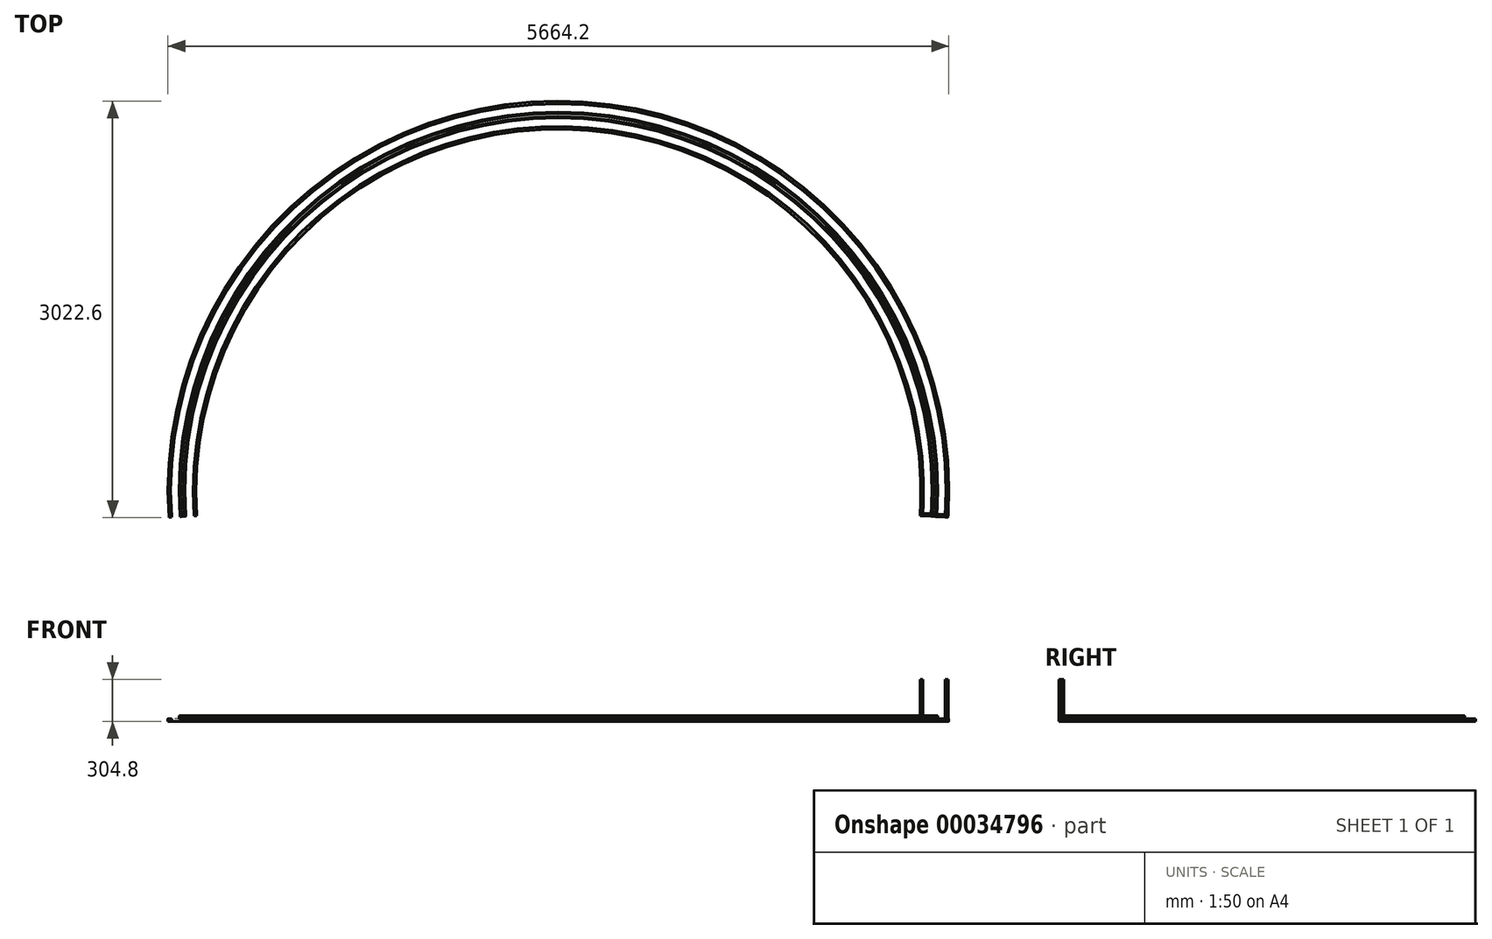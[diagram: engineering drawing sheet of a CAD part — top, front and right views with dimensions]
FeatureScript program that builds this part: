
annotation { "Feature Type Name" : "Feature", "Feature Type Description" : "" }
export const myFeature = defineFeature(function(context is Context, id is Id, definition is map)
    precondition{}
    {
        {
            var Q0;
            Q0=qCreatedBy(makeId("Top.planeOp"),FACE);
            var sketch = newSketch(context, id + "F0", { "sketchPlane" : qUnion([Q0])});
            skArc(sketch, "E0", {"start": v(2825.69, -190.5) * mm, "mid": v(0, 2832.1) * mm, "end": v(-2825.69, -190.5) * mm});
            skLineSegment(sketch, "E1", {"start": v(-2825.69, -190.5) * mm, "end": v(2825.69, -190.5) * mm, "construction": true});
            skLineSegment(sketch, "E2", {"start": v(-2622.95, -176.83) * mm, "end": v(-2641.95, -178.11) * mm});
            skLineSegment(sketch, "E3", {"start": v(2622.95, -176.83) * mm, "end": v(2641.95, -178.11) * mm});
            skArc(sketch, "E4", {"start": v(2806.68, -189.22) * mm, "mid": v(0, 2813.05) * mm, "end": v(-2806.68, -189.22) * mm});
            skArc(sketch, "E5", {"start": v(2622.95, -176.83) * mm, "mid": v(0, 2628.9) * mm, "end": v(-2622.95, -176.83) * mm});
            skArc(sketch, "E6", {"start": v(2641.95, -178.11) * mm, "mid": v(0, 2647.95) * mm, "end": v(-2641.95, -178.11) * mm});
            skLineSegment(sketch, "E7.trimOffspring", {"start": v(2806.68, -189.22) * mm, "end": v(2825.69, -190.5) * mm});
            skLineSegment(sketch, "E8.trimOffspring", {"start": v(-2806.68, -189.22) * mm, "end": v(-2825.69, -190.5) * mm});
            skLineSegment(sketch, "E9", {"start": v(-2806.68, -189.22) * mm, "end": v(-2641.95, -178.11) * mm, "construction": true});
            skLineSegment(sketch, "E10", {"start": v(-2622.95, -176.83) * mm, "end": v(0, 0) * mm, "construction": true});
            skLineSegment(sketch, "E11", {"start": v(0, 0) * mm, "end": v(2622.95, -176.83) * mm, "construction": true});
            skLineSegment(sketch, "E12", {"start": v(2641.95, -178.11) * mm, "end": v(2806.68, -189.22) * mm, "construction": true});
            skSolve(sketch);
        }
        {
            var Q0;
            Q0 = qSketchRegion(id + "F0", true);
            extrude(context, id + "F1", {"entities" : qUnion([Q0]), "depth" : 19.05 * mm});
        }
        {
            var Q0;
            Q0=makeQuery(id+"F1.opExtrude","SWEPT_FACE",FACE,{"disambiguationData":[OSD([sQuery(id+"F0.wireOp",EDGE,"E3")])]});
            var sketch = newSketch(context, id + "F2", { "sketchPlane" : qUnion([Q0])});
            skLineSegment(sketch, "E13.bottom", {"start": v(2647.95, 0) * mm, "end": v(2813.05, 0) * mm});
            skLineSegment(sketch, "E13.top", {"start": v(2647.95, 19.05) * mm, "end": v(2813.05, 19.05) * mm});
            skLineSegment(sketch, "E13.left", {"start": v(2647.95, 0) * mm, "end": v(2647.95, 19.05) * mm});
            skLineSegment(sketch, "E13.right", {"start": v(2813.05, 0) * mm, "end": v(2813.05, 19.05) * mm});
            skLineSegment(sketch, "E14.bottom", {"start": v(2647.95, 19.05) * mm, "end": v(2628.9, 19.05) * mm});
            skLineSegment(sketch, "E14.top", {"start": v(2647.95, 304.8) * mm, "end": v(2628.9, 304.8) * mm});
            skLineSegment(sketch, "E14.left", {"start": v(2647.95, 19.05) * mm, "end": v(2647.95, 304.8) * mm});
            skLineSegment(sketch, "E14.right", {"start": v(2628.9, 19.05) * mm, "end": v(2628.9, 304.8) * mm});
            skLineSegment(sketch, "E15.bottom", {"start": v(2813.05, 19.05) * mm, "end": v(2832.1, 19.05) * mm});
            skLineSegment(sketch, "E15.top", {"start": v(2813.05, 304.8) * mm, "end": v(2832.1, 304.8) * mm});
            skLineSegment(sketch, "E15.left", {"start": v(2813.05, 19.05) * mm, "end": v(2813.05, 304.8) * mm});
            skLineSegment(sketch, "E15.right", {"start": v(2832.1, 19.05) * mm, "end": v(2832.1, 304.8) * mm});
            skSolve(sketch);
        }
        {
            var Q0;
            Q0 = qSketchRegion(id + "F2", true);
            extrude(context, id + "F3", {"entities" : qUnion([Q0]), "oppositeDirection" : true, "depth" : 19.05 * mm});
        }
        {
            var Q0;
            Q0=makeQuery(id+"F1.opExtrude","CAP_FACE",FACE,{"disambiguationData":[OSD([sQuery(id+"F0.wireOp",EDGE,"E2"),sQuery(id+"F0.wireOp",EDGE,"E3"),sQuery(id+"F0.wireOp",EDGE,"E5"),sQuery(id+"F0.wireOp",EDGE,"E6")])],"isStart":false});
            var sketch = newSketch(context, id + "F4", { "sketchPlane" : qUnion([Q0])});
            skArc(sketch, "E16", {"start": v(2724.32, -183.67) * mm, "mid": v(0, 2730.5) * mm, "end": v(-2724.32, -183.67) * mm});
            skLineSegment(sketch, "E17", {"start": v(2641.95, -178.11) * mm, "end": v(2724.32, -183.67) * mm, "construction": true});
            skLineSegment(sketch, "E18", {"start": v(2724.32, -183.67) * mm, "end": v(2806.68, -189.22) * mm, "construction": true});
            skLineSegment(sketch, "E19", {"start": v(-2641.95, -178.11) * mm, "end": v(-2806.68, -189.22) * mm, "construction": true});
            skSolve(sketch);
        }
        {
            var Q0;
            Q0=makeQuery(id+"F3.opExtrude","CAP_FACE",FACE,{"disambiguationData":[OSD([sQuery(id+"F2.wireOp",EDGE,"E13.bottom"),sQuery(id+"F2.wireOp",EDGE,"E13.top"),sQuery(id+"F2.wireOp",EDGE,"E13.left"),sQuery(id+"F2.wireOp",EDGE,"E13.right")])],"isStart":true});
            var sketch = newSketch(context, id + "F5", { "sketchPlane" : qUnion([Q0])});
            skLineSegment(sketch, "E20", {"start": v(2713.04, 19.05) * mm, "end": v(2747.96, 19.05) * mm});
            skLineSegment(sketch, "E21", {"start": v(2751.14, 22.22) * mm, "end": v(2751.14, 36.51) * mm});
            skLineSegment(sketch, "E22", {"start": v(2746.38, 41.28) * mm, "end": v(2746.38, 41.28) * mm});
            skLineSegment(sketch, "E23", {"start": v(2741.61, 36.51) * mm, "end": v(2741.61, 34.13) * mm});
            skLineSegment(sketch, "E24", {"start": v(2719.39, 34.13) * mm, "end": v(2719.39, 36.51) * mm});
            skLineSegment(sketch, "E25", {"start": v(2714.63, 41.28) * mm, "end": v(2714.63, 41.28) * mm});
            skLineSegment(sketch, "E26", {"start": v(2709.86, 36.51) * mm, "end": v(2709.86, 22.22) * mm});
            skPoint(sketch, "E27.visualSharp", {"position": v(2709.86, 41.28) * mm});
            skArc(sketch, "E27.filletArc", {"start": v(2714.63, 41.28) * mm, "mid": v(2711.26, 39.88) * mm, "end": v(2709.86, 36.51) * mm});
            skPoint(sketch, "E28.visualSharp", {"position": v(2741.61, 41.28) * mm});
            skArc(sketch, "E28.filletArc", {"start": v(2746.38, 41.28) * mm, "mid": v(2743, 39.88) * mm, "end": v(2741.61, 36.51) * mm});
            skPoint(sketch, "E29.visualSharp", {"position": v(2751.14, 41.28) * mm});
            skArc(sketch, "E29.filletArc", {"start": v(2751.14, 36.51) * mm, "mid": v(2749.74, 39.88) * mm, "end": v(2746.38, 41.28) * mm});
            skPoint(sketch, "E30.visualSharp", {"position": v(2719.39, 41.28) * mm});
            skArc(sketch, "E30.filletArc", {"start": v(2719.39, 36.51) * mm, "mid": v(2718, 39.88) * mm, "end": v(2714.63, 41.28) * mm});
            skPoint(sketch, "E31.visualSharp", {"position": v(2709.86, 19.05) * mm});
            skArc(sketch, "E31.filletArc", {"start": v(2709.86, 22.22) * mm, "mid": v(2710.8, 19.98) * mm, "end": v(2713.04, 19.05) * mm});
            skPoint(sketch, "E32.visualSharp", {"position": v(2751.14, 19.05) * mm});
            skArc(sketch, "E32.filletArc", {"start": v(2747.96, 19.05) * mm, "mid": v(2750.2, 19.98) * mm, "end": v(2751.14, 22.22) * mm});
            skLineSegment(sketch, "E33", {"start": v(2730.5, 19.05) * mm, "end": v(2730.5, 41.28) * mm, "construction": true});
            skLineSegment(sketch, "E34.0", {"start": v(2744.28, 36.51) * mm, "end": v(2744.28, 34.13) * mm});
            skLineSegment(sketch, "E34.1", {"start": v(2712.53, 36.51) * mm, "end": v(2712.53, 22.22) * mm});
            skArc(sketch, "E34.2", {"start": v(2714.63, 38.6) * mm, "mid": v(2713.14, 38) * mm, "end": v(2712.53, 36.51) * mm});
            skArc(sketch, "E34.3", {"start": v(2716.72, 36.51) * mm, "mid": v(2716.1, 38) * mm, "end": v(2714.63, 38.6) * mm});
            skLineSegment(sketch, "E34.4", {"start": v(2716.72, 34.13) * mm, "end": v(2716.72, 36.51) * mm});
            skArc(sketch, "E34.5", {"start": v(2712.53, 22.22) * mm, "mid": v(2712.68, 21.87) * mm, "end": v(2713.04, 21.72) * mm});
            skLineSegment(sketch, "E34.6", {"start": v(2713.04, 21.72) * mm, "end": v(2747.96, 21.72) * mm});
            skArc(sketch, "E34.7", {"start": v(2747.96, 21.72) * mm, "mid": v(2748.32, 21.87) * mm, "end": v(2748.47, 22.22) * mm});
            skLineSegment(sketch, "E34.8", {"start": v(2748.47, 22.22) * mm, "end": v(2748.47, 36.51) * mm});
            skArc(sketch, "E34.9", {"start": v(2748.47, 36.51) * mm, "mid": v(2747.86, 38) * mm, "end": v(2746.38, 38.6) * mm});
            skArc(sketch, "E34.10", {"start": v(2746.38, 38.6) * mm, "mid": v(2744.9, 38) * mm, "end": v(2744.28, 36.51) * mm});
            skLineSegment(sketch, "E35", {"start": v(2716.72, 34.13) * mm, "end": v(2719.39, 34.13) * mm});
            skLineSegment(sketch, "E36", {"start": v(2744.28, 34.13) * mm, "end": v(2741.61, 34.13) * mm});
            skSolve(sketch);
        }
        {
            var Q0;
            Q0=makeQuery(id+"F5.imprint","IMPRINT",FACE,{"disambiguationData":[TD([[makeQuery(id+"F5.imprint","IMPRINT",EDGE,{"derivedFrom":sQuery(id+"F5.wireOp",EDGE,"E20")}),1.0]])]});
            var Q1;
            Q1=sQuery(id+"F4.wireOp",EDGE,"E16");
            sweep(context, id + "F6", {"profiles" : qUnion([Q0]), "path" : qUnion([Q1])});
        }
        {
            var Q0;
            Q0=makeQuery(id+"F1.opExtrude","CAP_FACE",FACE,{"disambiguationData":[OSD([sQuery(id+"F0.wireOp",EDGE,"E2"),sQuery(id+"F0.wireOp",EDGE,"E3"),sQuery(id+"F0.wireOp",EDGE,"E5"),sQuery(id+"F0.wireOp",EDGE,"E6")])],"isStart":false});
            var sketch = newSketch(context, id + "F7", { "sketchPlane" : qUnion([Q0])});
            skLineSegment(sketch, "E37", {"start": v(2646.84, -76.51) * mm, "end": v(2646.86, 75.89) * mm});
            skLineSegment(sketch, "E38", {"start": v(2646.86, 75.89) * mm, "end": v(2627.8, 75.89) * mm});
            skLineSegment(sketch, "E39", {"start": v(2627.8, 75.89) * mm, "end": v(2627.79, -76.51) * mm});
            skLineSegment(sketch, "E40", {"start": v(2627.79, -76.51) * mm, "end": v(2646.84, -76.51) * mm});
            skSolve(sketch);
        }
        {
            var Q0;
            Q0=makeQuery(id+"F7.imprint","IMPRINT",FACE,{"disambiguationData":[TD([[makeQuery(id+"F7.imprint","IMPRINT",EDGE,{"derivedFrom":sQuery(id+"F7.wireOp",EDGE,"E37")}),1.0]])]});
            extrude(context, id + "F8", {"entities" : qUnion([Q0]), "operationType" : NewBodyOperationType.ADD, "depth" : 15.88 * mm});
        }
    });
